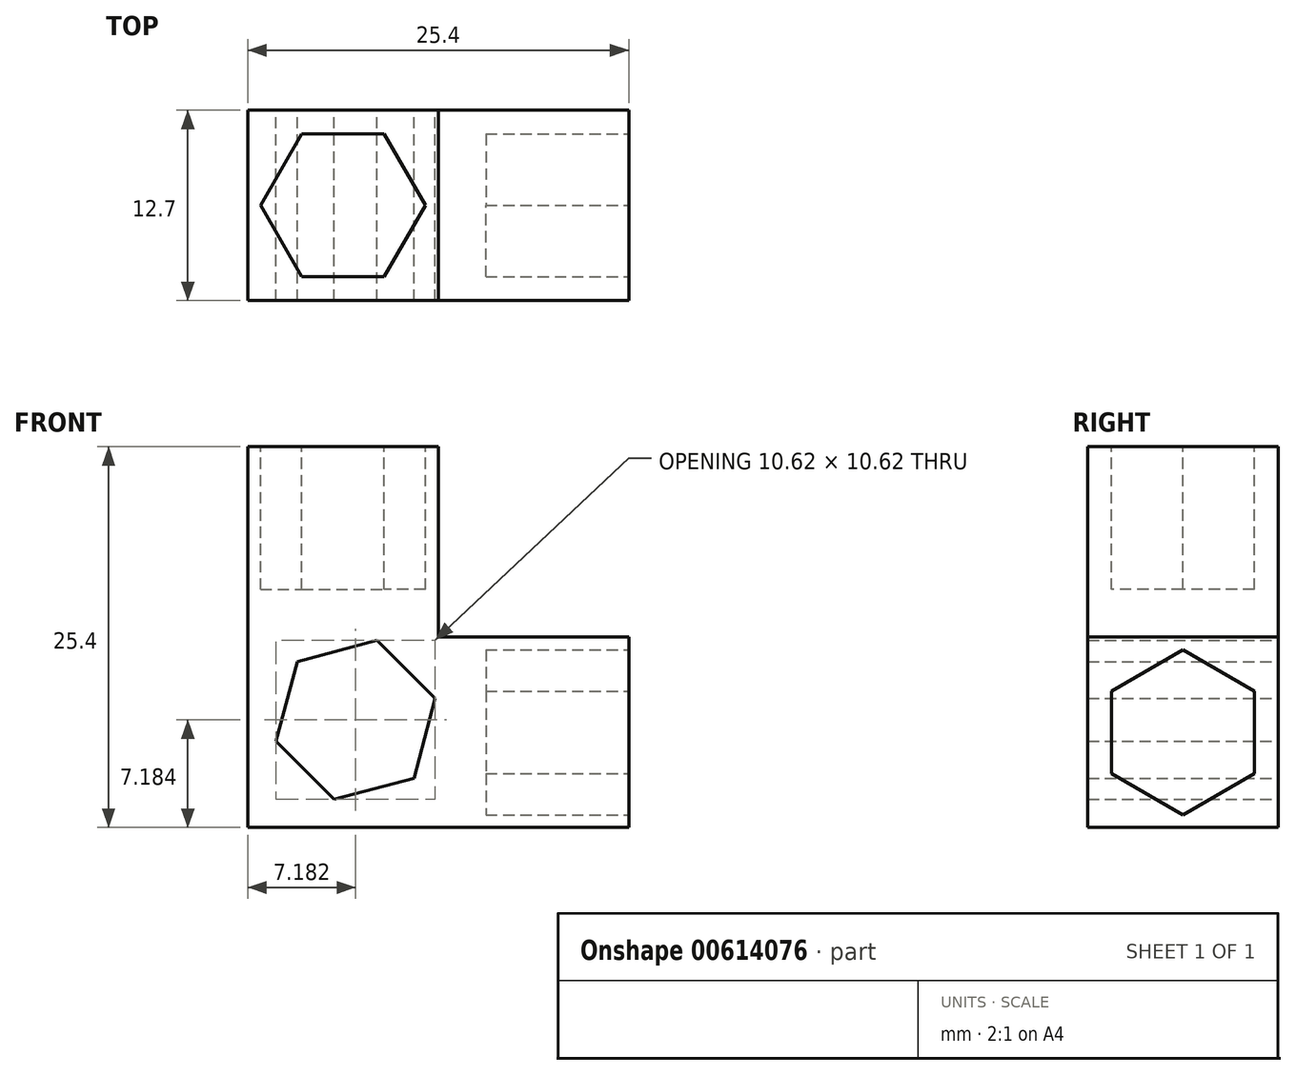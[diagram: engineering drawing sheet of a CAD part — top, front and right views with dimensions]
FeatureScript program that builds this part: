
annotation { "Feature Type Name" : "Feature", "Feature Type Description" : "" }
export const myFeature = defineFeature(function(context is Context, id is Id, definition is map)
    precondition{}
    {
        {
            var Q0;
            Q0=qCreatedBy(makeId("Front.planeOp"),FACE);
            var sketch = newSketch(context, id + "F0", { "sketchPlane" : qUnion([Q0])});
            skLineSegment(sketch, "E0", {"start": v(-14.86, 25.4) * mm, "end": v(-14.86, 0) * mm});
            skLineSegment(sketch, "E1", {"start": v(-14.86, 0) * mm, "end": v(10.54, 0) * mm});
            skLineSegment(sketch, "E2", {"start": v(10.54, 0) * mm, "end": v(10.54, 12.7) * mm});
            skLineSegment(sketch, "E3", {"start": v(10.54, 12.7) * mm, "end": v(-2.16, 12.7) * mm});
            skLineSegment(sketch, "E4", {"start": v(-2.16, 12.7) * mm, "end": v(-2.16, 25.4) * mm});
            skLineSegment(sketch, "E5", {"start": v(-2.16, 25.4) * mm, "end": v(-14.86, 25.4) * mm});
            skCircle(sketch, "E6.cCircle", {"center": v(-7.68, 7.18) * mm, "radius": 4.76 * mm, "construction": true});
            skLineSegment(sketch, "E6.0", {"start": v(-2.37, 8.6) * mm, "end": v(-3.79, 3.3) * mm});
            skLineSegment(sketch, "E6.1", {"start": v(-3.79, 3.3) * mm, "end": v(-9.1, 1.87) * mm});
            skLineSegment(sketch, "E6.2", {"start": v(-9.1, 1.87) * mm, "end": v(-12.99, 5.76) * mm});
            skLineSegment(sketch, "E6.3", {"start": v(-12.99, 5.76) * mm, "end": v(-11.57, 11.07) * mm});
            skLineSegment(sketch, "E6.4", {"start": v(-11.57, 11.07) * mm, "end": v(-6.25, 12.5) * mm});
            skLineSegment(sketch, "E6.5", {"start": v(-6.25, 12.5) * mm, "end": v(-2.37, 8.6) * mm});
            skPoint(sketch, "E6.0.midPoint", {"position": v(-3.08, 5.95) * mm});
            skLineSegment(sketch, "E7", {"start": v(-2.16, 25.4) * mm, "end": v(10.54, 12.7) * mm, "construction": true});
            skLineSegment(sketch, "E8", {"start": v(-14.86, 0) * mm, "end": v(-2.16, 12.7) * mm, "construction": true});
            skSolve(sketch);
        }
        {
            var Q0;
            Q0=makeQuery(id+"F0.imprint","IMPRINT",FACE,{"disambiguationData":[TD([[makeQuery(id+"F0.imprint","IMPRINT",EDGE,{"derivedFrom":sQuery(id+"F0.wireOp",EDGE,"E0")}),1.0]])]});
            extrude(context, id + "F1", {"entities" : qUnion([Q0]), "depth" : 12.7 * mm, "offsetDistance" : 25.4 * mm});
        }
        {
            var Q0;
            Q0=makeQuery(id+"F1.opExtrude","SWEPT_FACE",FACE,{"disambiguationData":[OSD([sQuery(id+"F0.wireOp",EDGE,"E5")])]});
            var sketch = newSketch(context, id + "F2", { "sketchPlane" : qUnion([Q0])});
            skCircle(sketch, "E9.cCircle", {"center": v(-8.51, -6.35) * mm, "radius": 4.76 * mm, "construction": true});
            skLineSegment(sketch, "E9.0", {"start": v(-3.01, -6.35) * mm, "end": v(-5.76, -11.11) * mm});
            skLineSegment(sketch, "E9.1", {"start": v(-5.76, -11.11) * mm, "end": v(-11.26, -11.11) * mm});
            skLineSegment(sketch, "E9.2", {"start": v(-11.26, -11.11) * mm, "end": v(-14.01, -6.35) * mm});
            skLineSegment(sketch, "E9.3", {"start": v(-14.01, -6.35) * mm, "end": v(-11.26, -1.59) * mm});
            skLineSegment(sketch, "E9.4", {"start": v(-11.26, -1.59) * mm, "end": v(-5.76, -1.59) * mm});
            skLineSegment(sketch, "E9.5", {"start": v(-5.76, -1.59) * mm, "end": v(-3.01, -6.35) * mm});
            skPoint(sketch, "E9.0.midPoint", {"position": v(-4.39, -8.73) * mm});
            skSolve(sketch);
        }
        {
            var Q0;
            Q0=makeQuery(id+"F2.imprint","IMPRINT",FACE,{"disambiguationData":[TD([[makeQuery(id+"F2.imprint","IMPRINT",EDGE,{"derivedFrom":sQuery(id+"F2.wireOp",EDGE,"73b03ed7-ce86-404d-a607-4e8877e6ee11.0")}),-1.0]])]});
            var Q1;
            Q1=makeQuery(id+"F2.imprint","IMPRINT",FACE,{"disambiguationData":[TD([[makeQuery(id+"F2.imprint","IMPRINT",EDGE,{"derivedFrom":sQuery(id+"F2.wireOp",EDGE,"E9.0")}),-1.0]])]});
            extrude(context, id + "F3", {"entities" : qUnion([Q0, Q1]), "operationType" : NewBodyOperationType.REMOVE, "oppositeDirection" : true, "depth" : 9.52 * mm, "offsetDistance" : 25.4 * mm});
        }
        {
            var Q0;
            Q0=makeQuery(id+"F1.opExtrude","SWEPT_FACE",FACE,{"disambiguationData":[OSD([sQuery(id+"F0.wireOp",EDGE,"E2")])]});
            var sketch = newSketch(context, id + "F4", { "sketchPlane" : qUnion([Q0])});
            skCircle(sketch, "E10.cCircle", {"center": v(-6.35, 6.35) * mm, "radius": 4.76 * mm, "construction": true});
            skLineSegment(sketch, "E10.0", {"start": v(-1.59, 3.6) * mm, "end": v(-6.35, 0.85) * mm});
            skLineSegment(sketch, "E10.1", {"start": v(-6.35, 0.85) * mm, "end": v(-11.11, 3.6) * mm});
            skLineSegment(sketch, "E10.2", {"start": v(-11.11, 3.6) * mm, "end": v(-11.11, 9.1) * mm});
            skLineSegment(sketch, "E10.3", {"start": v(-11.11, 9.1) * mm, "end": v(-6.35, 11.85) * mm});
            skLineSegment(sketch, "E10.4", {"start": v(-6.35, 11.85) * mm, "end": v(-1.59, 9.1) * mm});
            skLineSegment(sketch, "E10.5", {"start": v(-1.59, 9.1) * mm, "end": v(-1.59, 3.6) * mm});
            skPoint(sketch, "E10.0.midPoint", {"position": v(-3.97, 2.23) * mm});
            skSolve(sketch);
        }
        {
            var Q0;
            Q0=makeQuery(id+"F4.imprint","IMPRINT",FACE,{"disambiguationData":[TD([[makeQuery(id+"F4.imprint","IMPRINT",EDGE,{"derivedFrom":sQuery(id+"F4.wireOp",EDGE,"E10.0")}),-1.0]])]});
            extrude(context, id + "F5", {"entities" : qUnion([Q0]), "operationType" : NewBodyOperationType.REMOVE, "oppositeDirection" : true, "depth" : 9.52 * mm, "offsetDistance" : 25.4 * mm});
        }
    });
